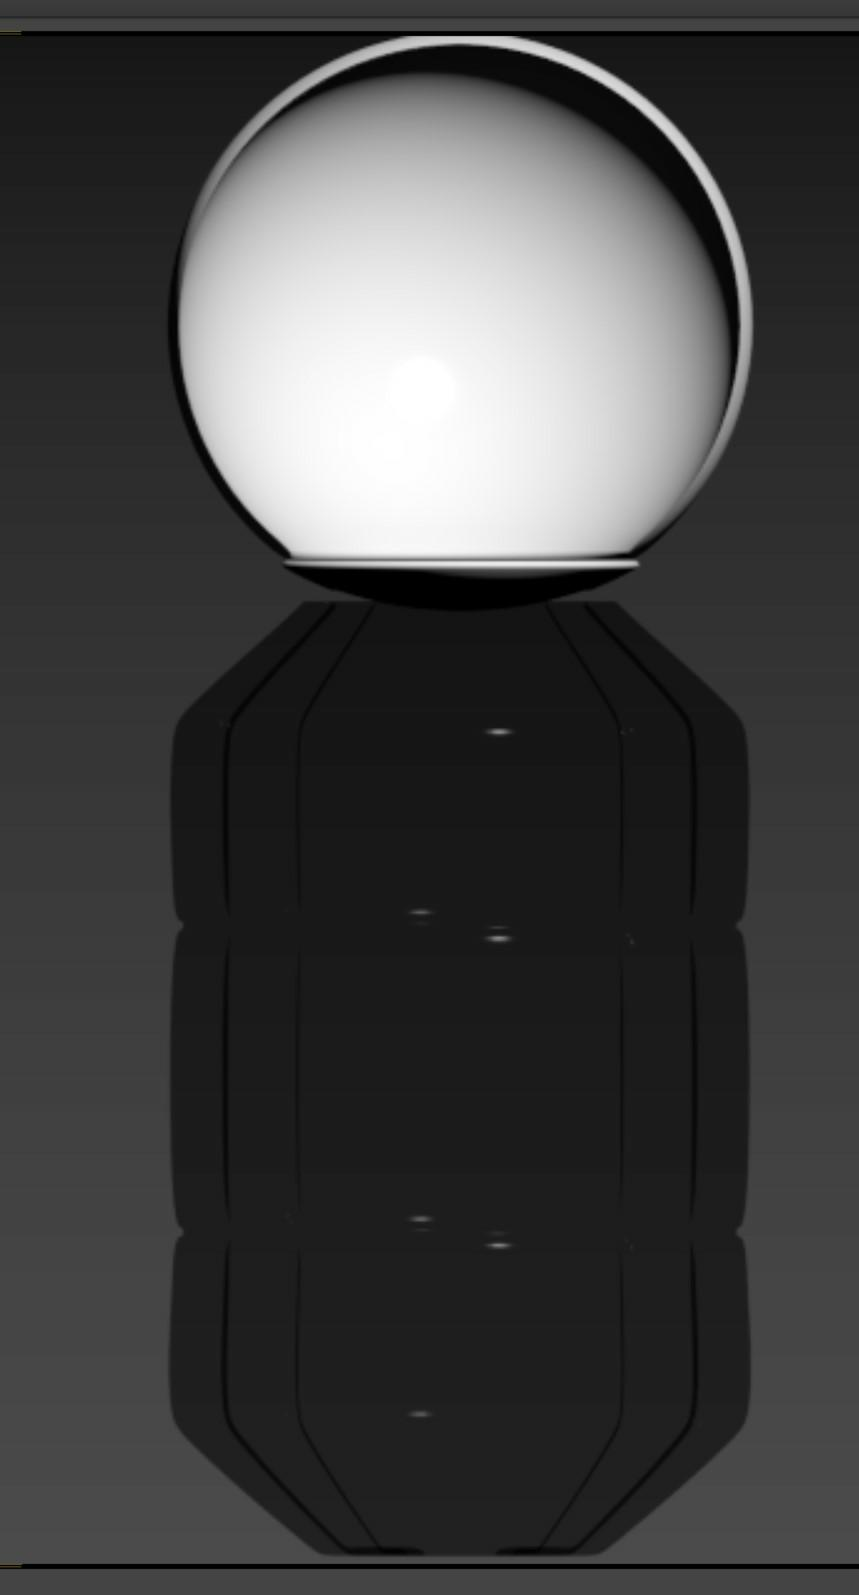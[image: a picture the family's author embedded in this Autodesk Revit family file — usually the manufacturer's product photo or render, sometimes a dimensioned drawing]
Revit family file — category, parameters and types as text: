
# Revit family: Navazi 4
name_source: partatom
category: Generic Models
units: mm (PartAtom-declared; Revit-internal decimal feet)

## family parameters
Can host rebar = No
Cut with Voids When Loaded = No
Host = Face
Part Type = Normal
Room Calculation Point = No
Round Connector Dimension = Use Diameter
Shared = No

## types (1)
- Navazi 4
    Default Elevation = 1219 mm
    Description = This beautiful collection NAVAZI combines contemporary design with traditional craftsmanship. 

The NAVAZI collection is perfect for any modern interior, providing a soft and warm illumination that creates a cozy and inviting atmosphere. It is ideal for use in the living room, dining room, or bedroom.

With its timeless design and impeccable craftsmanship, the NAVAZI collection is a true work of art that will enhance the beauty of any space. Whether you're looking to add a touch of elegance to your home or office, this stunning lighting fixture is sure to impress.
    Manufacturer = SVITANOK
    URL = https://svitanok.com

## geometry (parser evidence)
native form markers: Sweep x7
no freeform markers — native parametric forms only
